# Revit family: IS_Tesi_T3545_BIM_GB
name_source: partatom
category: Plumbing Fixtures
revit_build: Autodesk Revit MEP 2014 (Build: 20130308_1515(x64)
units: mm (PartAtom-declared; Revit-internal decimal feet)

## types (1)
- T354501-Tesi Wh Bowl Aquablade Hf
    Accessories = www.idealspec.co.uk
    AreaUnits = millimeters
    Assembly Code = C1030200
    AssetType = Fixed
    BIMObjectName = ISI_IdealStandard_WCPans_Tesi-WallHung_T3545
    BREEAMApproved = No
    Brand = Ideal Standard
    CWFU = 0
    CodePerformance = Vitreous china to BS 3402
    ConnectionType = Plumbing
    Cost = 0 $
    Default Elevation = 0 mm  [stored 0 ft]
    Description = Tesi wall mounted wc pan with hidden fixations
    DurationUnit = year
    ECA = No
    ExpectedLife = 30
    Features = Wall mounted wc pan with hidden fixations
    Finish = White
    HWFU = 0
    IfcExportAs = IfcSanitaryTerminalType
    IfcExportType = TOILETPAN
    InstallationInstructions = www.idealspec.co.uk/resources.html
    LinearUnits = millimeters
    ManufacturerURL = www.idealspec.co.uk
    Model = T354501
    ModelNumber = T354501
    ModelReference = Tesi wall mounted wc pan with hidden fixations
    NBSDescription = WC pans
    NBSReference = 45-30-70/384
    Name = WCPans_Tesi-WallHung_T3545_IdealStandard
    NettWeight = 22 Kg
    NominalDepth = 531 mm
    NominalHeight = 337 mm
    NominalLength = 531 mm
    NominalWidth = 366 mm
    PanColor = White
    PanMaterial = Vitreous china
    PanMounting = BackToWall
    ProductInformation = www.idealspec.co.uk/assets/datasheet/T354501
    Shape = Sculptured
    Size = 366 x 531 x 337 mm
    Space = Internal
    SpilloverLevel = 0 mm  [stored 0 ft]
    ToiletPanType = WashDown
    ToiletType = Other
    URL = www.idealspec.co.uk
    Uniclass2015Description = WC pans
    Uniclass2015Reference = Pr_40_20_93_94
    Uniclass2015Version = Products v1.1
    Version = 1
    VolumeUnits = Litres
    WFU = 0
    WRAS = No
    WarrantyDescription = Manufacturers Warranty
    WarrantyDurationParts = 99
    WarrantyDurationUnit = year
    WaterEfficientProduct = No

note: [stored X ft] marks values corroborated as IEEE doubles in the binary element streams (Revit-internal decimal feet)

## geometry (parser evidence)
native form markers: Sweep x5
no freeform markers — native parametric forms only
